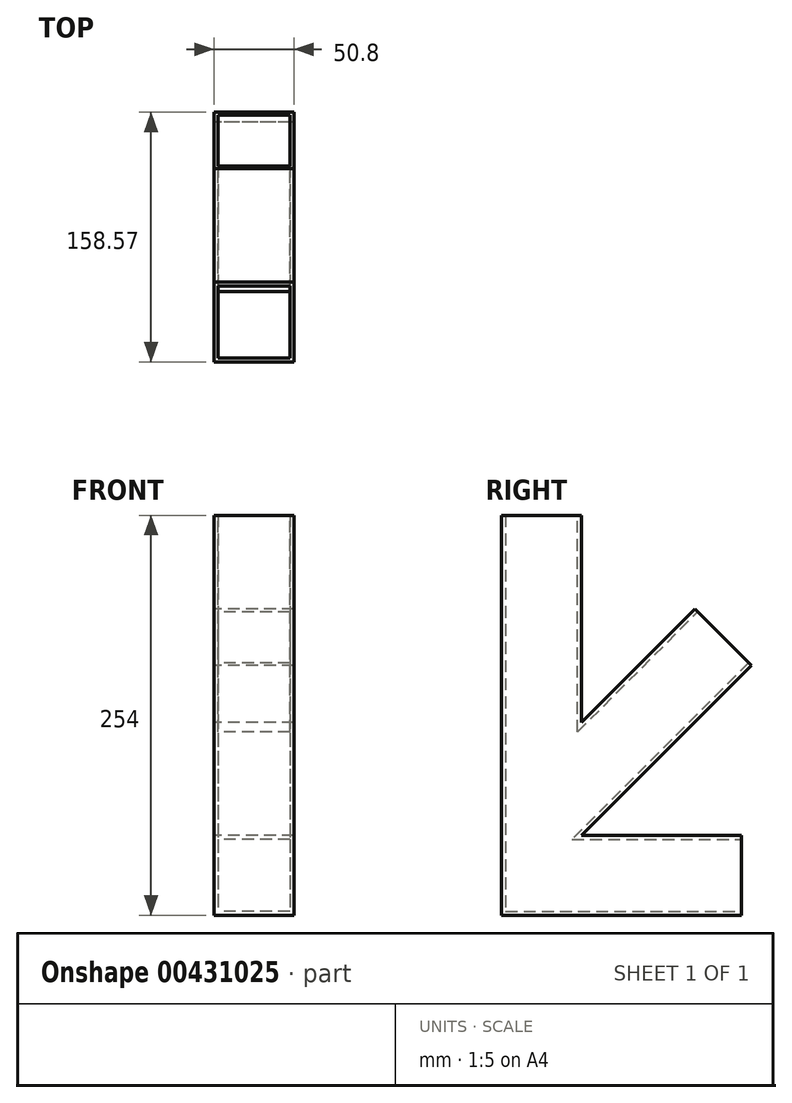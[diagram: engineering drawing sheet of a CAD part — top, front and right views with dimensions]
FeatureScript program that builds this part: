
annotation { "Feature Type Name" : "Feature", "Feature Type Description" : "" }
export const myFeature = defineFeature(function(context is Context, id is Id, definition is map)
    precondition{}
    {
        {
            var Q0;
            Q0=qCreatedBy(makeId("Right.planeOp"),FACE);
            var sketch = newSketch(context, id + "F0", { "sketchPlane" : qUnion([Q0])});
            skLineSegment(sketch, "E0.bottom", {"start": v(-16.5, 131.36) * mm, "end": v(34.3, 131.36) * mm});
            skLineSegment(sketch, "E0.top", {"start": v(-16.5, -122.64) * mm, "end": v(34.3, -122.64) * mm});
            skLineSegment(sketch, "E0.left", {"start": v(-16.5, 131.36) * mm, "end": v(-16.5, -122.64) * mm});
            skLineSegment(sketch, "E1", {"start": v(34.3, -71.84) * mm, "end": v(135.9, -71.84) * mm});
            skLineSegment(sketch, "E2", {"start": v(135.9, -71.84) * mm, "end": v(135.9, -122.64) * mm});
            skLineSegment(sketch, "E3", {"start": v(135.9, -122.64) * mm, "end": v(34.3, -122.64) * mm});
            skLineSegment(sketch, "E4", {"start": v(34.3, 0) * mm, "end": v(106.15, 71.84) * mm});
            skLineSegment(sketch, "E5", {"start": v(106.15, 71.84) * mm, "end": v(142.07, 35.92) * mm});
            skLineSegment(sketch, "E6", {"start": v(142.07, 35.92) * mm, "end": v(34.3, -71.84) * mm});
            skLineSegment(sketch, "E7", {"start": v(34.3, 0) * mm, "end": v(34.3, 131.36) * mm});
            skSolve(sketch);
        }
        {
            var Q0;
            Q0=makeQuery(id+"F0.imprint","IMPRINT",FACE,{"disambiguationData":[TD([[makeQuery(id+"F0.imprint","IMPRINT",EDGE,{"derivedFrom":sQuery(id+"F0.wireOp",EDGE,"E0.bottom")}),-1.0]])]});
            extrude(context, id + "F1", {"entities" : qUnion([Q0]), "depth" : 50.8 * mm});
        }
        {
            var Q0;
            Q0=makeQuery(id+"F1.opExtrude","SWEPT_FACE",FACE,{"disambiguationData":[OSD([sQuery(id+"F0.wireOp",EDGE,"E0.bottom")])]});
            var Q1;
            Q1=makeQuery(id+"F1.opExtrude","SWEPT_FACE",FACE,{"disambiguationData":[OSD([sQuery(id+"F0.wireOp",EDGE,"E5")])]});
            var Q2;
            Q2=makeQuery(id+"F1.opExtrude","SWEPT_FACE",FACE,{"disambiguationData":[OSD([sQuery(id+"F0.wireOp",EDGE,"E2")])]});
            shell(context, id + "F2", {"entities" : qUnion([Q0, Q1, Q2]), "thickness" : 2.54 * mm});
        }
    });
